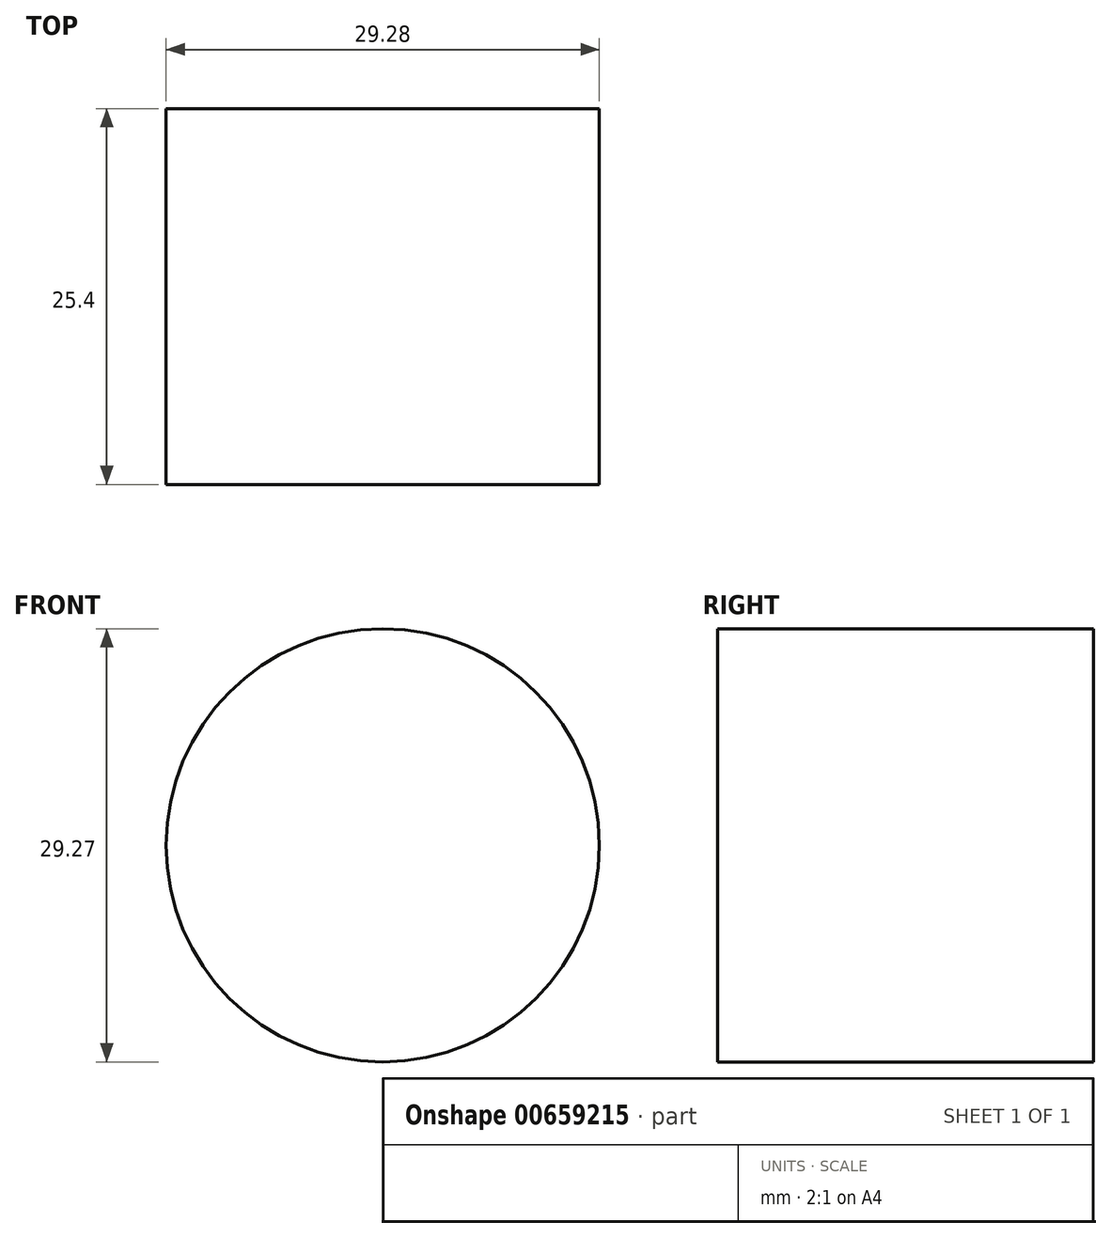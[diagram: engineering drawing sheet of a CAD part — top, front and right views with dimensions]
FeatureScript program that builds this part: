
annotation { "Feature Type Name" : "Feature", "Feature Type Description" : "" }
export const myFeature = defineFeature(function(context is Context, id is Id, definition is map)
    precondition{}
    {
        {
            var Q0;
            Q0=qCreatedBy(makeId("Front.planeOp"),FACE);
            var sketch = newSketch(context, id + "F0", { "sketchPlane" : qUnion([Q0])});
            skCircle(sketch, "E0", {"center": v(-42.17, 39.76) * mm, "radius": 15.65 * mm});
            skCircle(sketch, "E1", {"center": v(22.55, -20.48) * mm, "radius": 14.64 * mm});
            skSolve(sketch);
        }
        {
            var Q0;
            Q0=sQuery(id+"F0.wireOp",EDGE,"E1");
            extrude(context, id + "F1", {"bodyType" : ToolBodyType.SURFACE, "surfaceEntities" : qUnion([Q0]), "depth" : 25.4 * mm, "offsetDistance" : 25.4 * mm});
        }
    });
